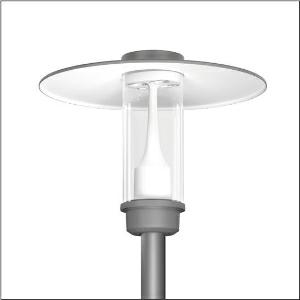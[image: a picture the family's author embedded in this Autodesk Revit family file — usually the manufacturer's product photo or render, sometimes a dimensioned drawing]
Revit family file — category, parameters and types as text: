
# Revit family: litepole_2_iq___p1_0a_5xa5425ff14h_a7e5
name_source: partatom
category: Lighting Fixtures
units: mm (PartAtom-declared; Revit-internal decimal feet)

## family parameters
Cut with Voids When Loaded = No
Host = Face
Light Source = No
Part Type = Normal
Room Calculation Point = No
Round Connector Dimension = Use Diameter
Shared = No

## types (1)
- --- (1 x LED, 1520 lm, 10.5 W, 3000K)
    Apparent Load = 11 VA
    CIE Flux Codes = 33 62 89 96 100
    Color Rendering = 70
    Color Temperature = 3000K
    Default Elevation = 1800 mm
    Description = Litepole 2 iQ, mast luminaire, Module 540 iQ-SR, primary light control with 3 zone facetted reflector, of plastic, silver coated, highly specular, structured, primary optical cover: cover, of PMMA, transparent, light distribution: P1.0a, light emission: direct distribution, primary light characteristic: strongly asymmetric, installation type: post-top, LED, High Power LED, rated luminous flux: 1.520lm, luminous efficacy: 145lm/W, light colour: 730, colour temperature: 3000K, control gear: ECG iQ, control: Auto-Match, Temp-Guard, Lumen-Switch, Night-Set, Smart-Wire, Light-Fading, Desk-Remote (wireless, voltage-free reading and setting of iQ features in the workshop via application-optimized NFC function/RFID function), optimised constant luminous flux control (CLO 2.0), Street-Remote, presetting dimming logarithmic, with terminal, 6-pole, max. 2.5mm², mains connection: 230..240V, AC, 50/60Hz, start of lifetime: 11W, end of service life: 11W, reduction: 5W, luminaire housing, upper part, of aluminium, coated, Siteco® metallic grey (DB 702S), diameter: 750mm, height: 590mm, spigot size: d x l = 76 x 70mm (post-top) | with reducer (optional accessory) 60 x 70mm, post-top mast mounting element, of diecast aluminium, coated, Siteco® metallic grey (DB 702S), Module 540 iQ-SR, traffic white (RAL 9016), equipment: standard, protection rating (complete): IP65, insulation class (complete): insulation class II (safety insulation), certification: CE, ENEC, VDE, packaging unit: 1 piece

Light Distribution: P1.0a
    Height = 590 mm
    Lamp = 1 x LED
    Lamp Light Flux = 1520 lm
    Lamp Power = 10.5 W
    Lamp count = 1
    Length = 750 mm
    Luminous efficacy = 145 lm/W
    Manufacturer = Siteco
    ModVariant = No
    Model = 5XA5425FF14H
    Number of Poles = 1
    OnlyDefault = Yes
    Power Factor = 1
    Product Name = Litepole 2 iQ | P1.0a
    Product group = mast luminaire | pylon top
    ProductGroupID = 6100
    Protection Class = Protection class II
    Protection Degree = IP 65
    RLX_Detail_Level = 1
    RLX_Emergency_Light_Flux = 0 lm
    RLX_Emergency_Type = 0
    RLX_Emergency_Type_DB = No
    RlxData = <blob elided: 138825 chars, md5=309b9c56>
    Socket = socket
    Standby Power = 0 W
    System Light Flux = 1520 lm
    System Power = 11 W
    Type Comments = factory setting: luminous flux: 100 % | dim-lin: 254 | 419 mA
    Type Image = l_1006518.jpg
    URL = http://relux.com
    VarID = @adj_126825
    Voltage = 0 V
    Weight = 0.00 kg
    Width = 0 mm  [stored 0 ft]

note: [stored X ft] marks values corroborated as IEEE doubles in the binary element streams (Revit-internal decimal feet)

## geometry (parser evidence)
native form markers: Blend x4, Sweep x12
no freeform markers — native parametric forms only
